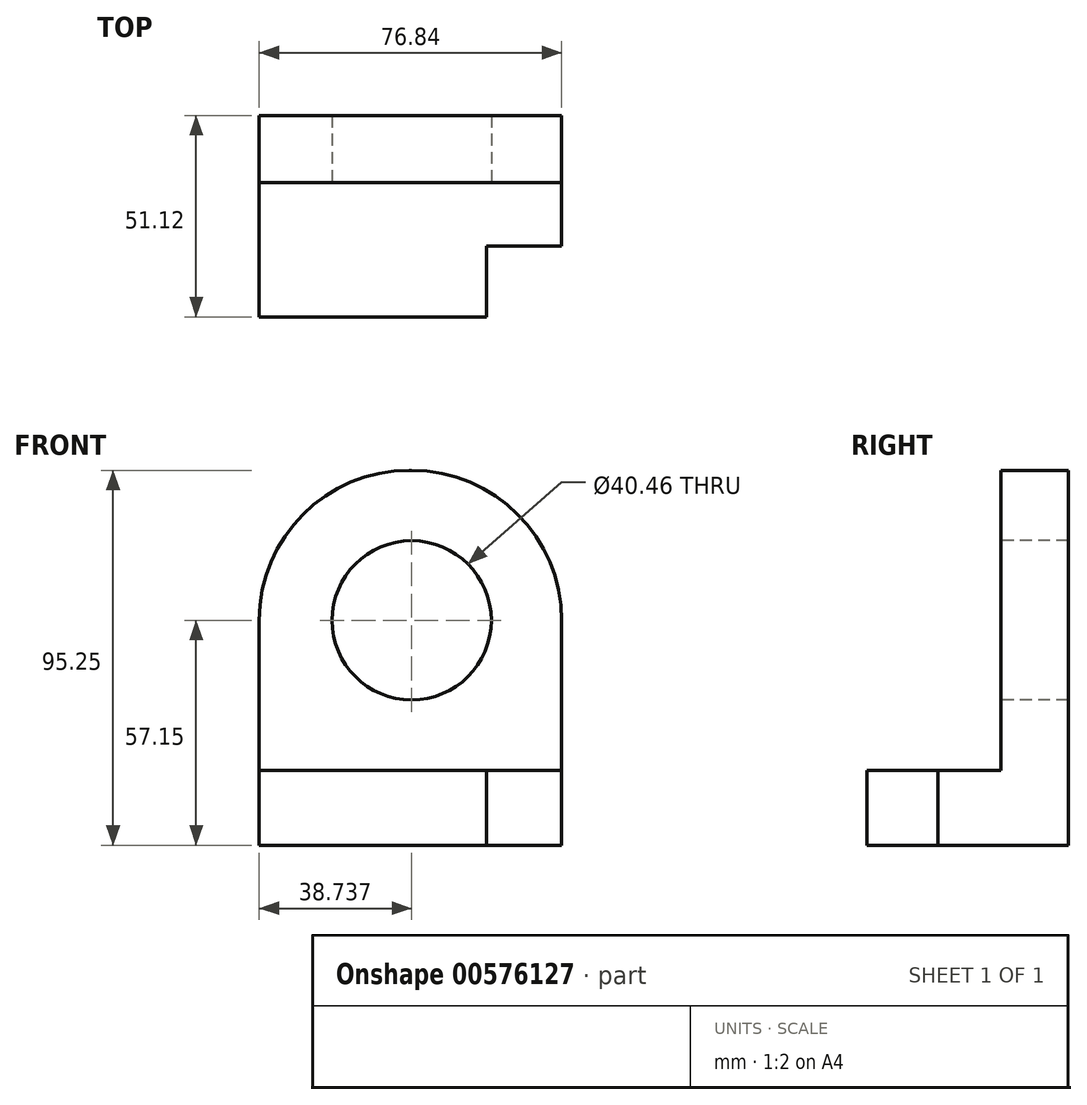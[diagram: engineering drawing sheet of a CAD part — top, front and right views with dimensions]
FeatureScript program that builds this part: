
annotation { "Feature Type Name" : "Feature", "Feature Type Description" : "" }
export const myFeature = defineFeature(function(context is Context, id is Id, definition is map)
    precondition{}
    {
        {
            var Q0;
            Q0=qCreatedBy(makeId("Top.planeOp"),FACE);
            var sketch = newSketch(context, id + "F0", { "sketchPlane" : qUnion([Q0])});
            skLineSegment(sketch, "E0.bottom", {"start": v(-38.42, 25.56) * mm, "end": v(38.42, 25.56) * mm});
            skLineSegment(sketch, "E0.top", {"start": v(-38.42, -25.56) * mm, "end": v(38.42, -25.56) * mm});
            skLineSegment(sketch, "E0.left", {"start": v(-38.42, 25.56) * mm, "end": v(-38.42, -25.56) * mm});
            skLineSegment(sketch, "E0.right", {"start": v(38.42, 25.56) * mm, "end": v(38.42, -25.56) * mm});
            skPoint(sketch, "E0.middle", {"position": v(0, 0) * mm});
            skSolve(sketch);
        }
        {
            var Q0;
            Q0 = qSketchRegion(id + "F0", true);
            extrude(context, id + "F1", {"entities" : qUnion([Q0]), "depth" : 19.05 * mm, "offsetDistance" : 25.4 * mm});
        }
        {
            var Q0;
            Q0=makeQuery(id+"F1.opExtrude","CAP_FACE",FACE,{"disambiguationData":[OSD([sQuery(id+"F0.wireOp",EDGE,"E0.bottom"),sQuery(id+"F0.wireOp",EDGE,"E0.top"),sQuery(id+"F0.wireOp",EDGE,"E0.left"),sQuery(id+"F0.wireOp",EDGE,"E0.right")])],"isStart":false});
            var sketch = newSketch(context, id + "F2", { "sketchPlane" : qUnion([Q0])});
            skLineSegment(sketch, "E1.bottom", {"start": v(38.42, -25.56) * mm, "end": v(19.36, -25.56) * mm});
            skLineSegment(sketch, "E1.top", {"start": v(38.42, -7.53) * mm, "end": v(19.36, -7.53) * mm});
            skLineSegment(sketch, "E1.left", {"start": v(38.42, -25.56) * mm, "end": v(38.42, -7.53) * mm});
            skLineSegment(sketch, "E1.right", {"start": v(19.36, -25.56) * mm, "end": v(19.36, -7.53) * mm});
            skSolve(sketch);
        }
        {
            var Q0;
            Q0=makeQuery(id+"F2.imprint","IMPRINT",FACE,{"disambiguationData":[TD([[makeQuery(id+"F2.imprint","IMPRINT",EDGE,{"derivedFrom":sQuery(id+"F2.wireOp",EDGE,"E1.bottom")}),1.0]])]});
            extrude(context, id + "F3", {"entities" : qUnion([Q0]), "operationType" : NewBodyOperationType.REMOVE, "oppositeDirection" : true, "depth" : 22.6 * mm, "offsetDistance" : 25.4 * mm});
        }
        {
            var Q0;
            Q0=makeQuery(id+"F1.opExtrude","CAP_FACE",FACE,{"disambiguationData":[OSD([sQuery(id+"F0.wireOp",EDGE,"E0.bottom"),sQuery(id+"F0.wireOp",EDGE,"E0.top"),sQuery(id+"F0.wireOp",EDGE,"E0.left"),sQuery(id+"F0.wireOp",EDGE,"E0.right")])],"isStart":false});
            var sketch = newSketch(context, id + "F4", { "sketchPlane" : qUnion([Q0])});
            skLineSegment(sketch, "E2.bottom", {"start": v(-38.42, 25.56) * mm, "end": v(38.42, 25.56) * mm});
            skLineSegment(sketch, "E2.top", {"start": v(-38.42, 8.5) * mm, "end": v(38.42, 8.5) * mm});
            skLineSegment(sketch, "E2.left", {"start": v(-38.42, 25.56) * mm, "end": v(-38.42, 8.5) * mm});
            skLineSegment(sketch, "E2.right", {"start": v(38.42, 25.56) * mm, "end": v(38.42, 8.5) * mm});
            skLineSegment(sketch, "E3", {"start": v(381.94, 36.17) * mm, "end": v(381.94, -5.72) * mm});
            skSolve(sketch);
        }
        {
            var Q0;
            Q0 = qSketchRegion(id + "F4", true);
            extrude(context, id + "F5", {"entities" : qUnion([Q0]), "operationType" : NewBodyOperationType.ADD, "depth" : 76.2 * mm, "offsetDistance" : 25.4 * mm});
        }
        {
            var Q0;
            Q0=makeQuery(id+"F5.opExtrude","CAP_EDGE",EDGE,{"disambiguationData":[OSD([sQuery(id+"F4.wireOp",EDGE,"E2.left")])],"isStart":false});
            var Q1;
            Q1=makeQuery(id+"F5.opExtrude","CAP_EDGE",EDGE,{"disambiguationData":[OSD([sQuery(id+"F4.wireOp",EDGE,"E2.right")])],"isStart":false});
            fillet(context, id + "F6", {"entities" : qUnion([Q0, Q1]), "radius" : 38.1 * mm, "tangentPropagation" : true, "allowEdgeOverflow" : false});
        }
        {
            var Q0;
            Q0=makeQuery(id+"F5.opExtrude","SWEPT_FACE",FACE,{"disambiguationData":[OSD([sQuery(id+"F4.wireOp",EDGE,"E2.top")])]});
            var sketch = newSketch(context, id + "F7", { "sketchPlane" : qUnion([Q0])});
            skCircle(sketch, "E4", {"center": v(0.32, 57.15) * mm, "radius": 20.23 * mm});
            skSolve(sketch);
        }
        {
            var Q0;
            Q0 = qSketchRegion(id + "F7", true);
            extrude(context, id + "F8", {"entities" : qUnion([Q0]), "operationType" : NewBodyOperationType.REMOVE, "oppositeDirection" : true, "depth" : 25.4 * mm, "offsetDistance" : 25.4 * mm});
        }
    });
